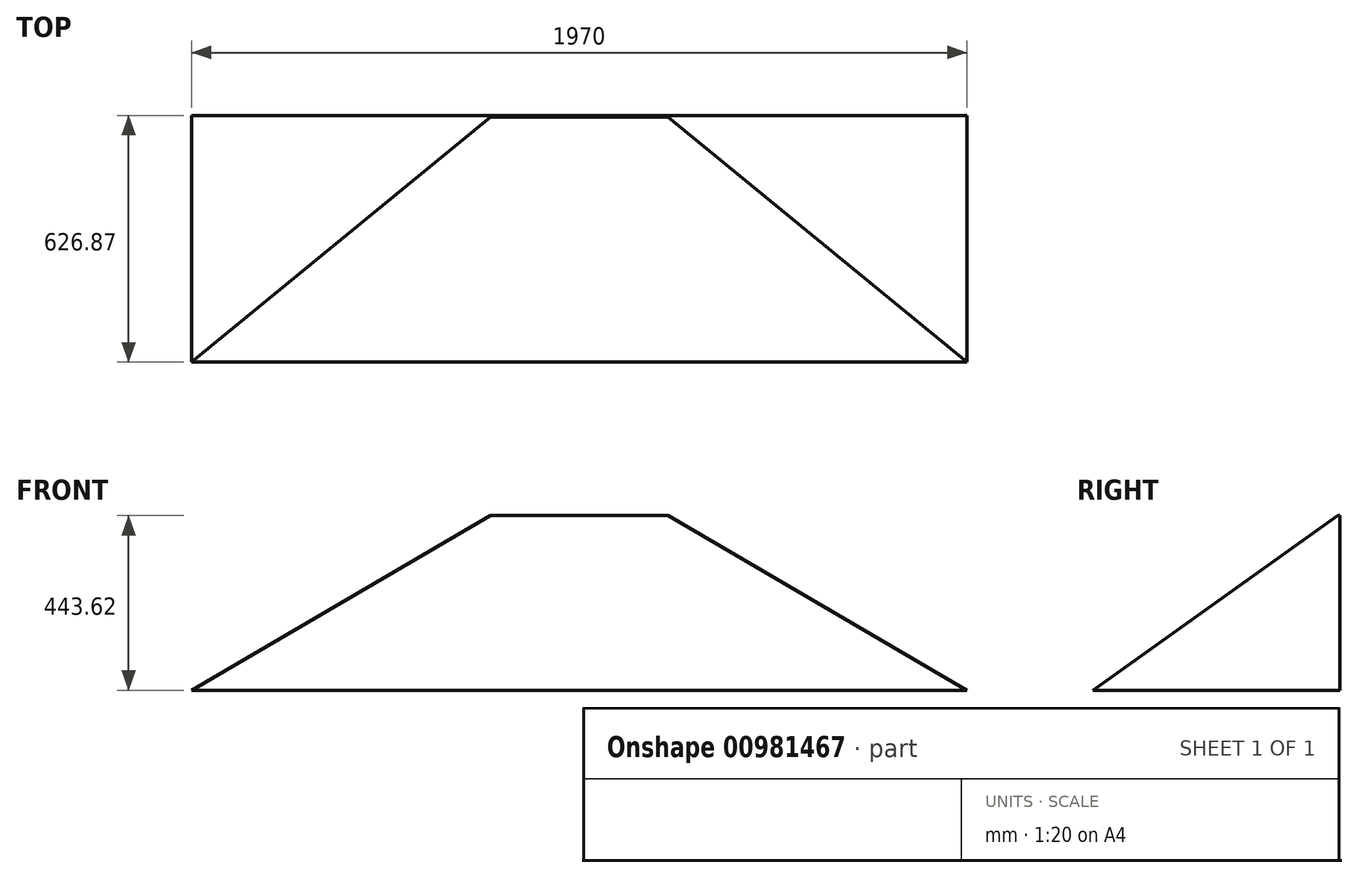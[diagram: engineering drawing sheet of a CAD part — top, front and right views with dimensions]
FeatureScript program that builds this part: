
annotation { "Feature Type Name" : "Feature", "Feature Type Description" : "" }
export const myFeature = defineFeature(function(context is Context, id is Id, definition is map)
    precondition{}
    {
        {
            var Q0;
            Q0=qCreatedBy(makeId("Front.planeOp"),FACE);
            var sketch = newSketch(context, id + "F0", { "sketchPlane" : qUnion([Q0])});
            skLineSegment(sketch, "E0", {"start": v(-839.6, -342.94) * mm, "end": v(1130.4, -342.94) * mm});
            skLineSegment(sketch, "E1", {"start": v(1130.4, -342.94) * mm, "end": v(370.4, 100.68) * mm});
            skLineSegment(sketch, "E2", {"start": v(370.4, 100.68) * mm, "end": v(-79.6, 100.68) * mm});
            skLineSegment(sketch, "E3", {"start": v(-79.6, 100.68) * mm, "end": v(-839.6, -342.94) * mm});
            skSolve(sketch);
        }
        {
            var Q0;
            Q0 = qSketchRegion(id + "F0", true);
            extrude(context, id + "F1", {"entities" : qUnion([Q0]), "depth" : 628 * mm, "offsetDistance" : 25 * mm});
        }
        {
            var Q0;
            Q0=qCreatedBy(makeId("Right.planeOp"),FACE);
            var sketch = newSketch(context, id + "F2", { "sketchPlane" : qUnion([Q0])});
            skLineSegment(sketch, "E4", {"start": v(0, 103.9) * mm, "end": v(-632.28, -346.8) * mm});
            skLineSegment(sketch, "E5", {"start": v(-632.28, -346.8) * mm, "end": v(-632.28, 103.9) * mm});
            skLineSegment(sketch, "E6", {"start": v(-632.28, 103.9) * mm, "end": v(0, 103.9) * mm});
            skSolve(sketch);
        }
        {
            var Q0;
            Q0=makeQuery(id+"F2.imprint","IMPRINT",FACE,{"disambiguationData":[TD([[makeQuery(id+"F2.imprint","IMPRINT",EDGE,{"derivedFrom":sQuery(id+"F2.wireOp",EDGE,"E4")}),-1.0]])]});
            var Q1;
            Q1=makeQuery(id+"F1.opExtrude","SWEPT_BODY",BODY,{"disambiguationData":[OSD([sQuery(id+"F0.wireOp",EDGE,"E0"),sQuery(id+"F0.wireOp",EDGE,"E1"),sQuery(id+"F0.wireOp",EDGE,"E2"),sQuery(id+"F0.wireOp",EDGE,"E3")])]});
            extrude(context, id + "F3", {"entities" : qUnion([Q0]), "operationType" : NewBodyOperationType.REMOVE, "endBound" : BoundingType.THROUGH_ALL, "depth" : 2000 * mm, "offsetDistance" : 25 * mm, "hasSecondDirection" : true, "secondDirectionBound" : SecondDirectionBoundingType.THROUGH_ALL, "secondDirectionOppositeDirection" : true, "secondDirectionDepth" : 1200 * mm, "secondDirectionBoundEntityBody" : qUnion([Q1])});
        }
    });
